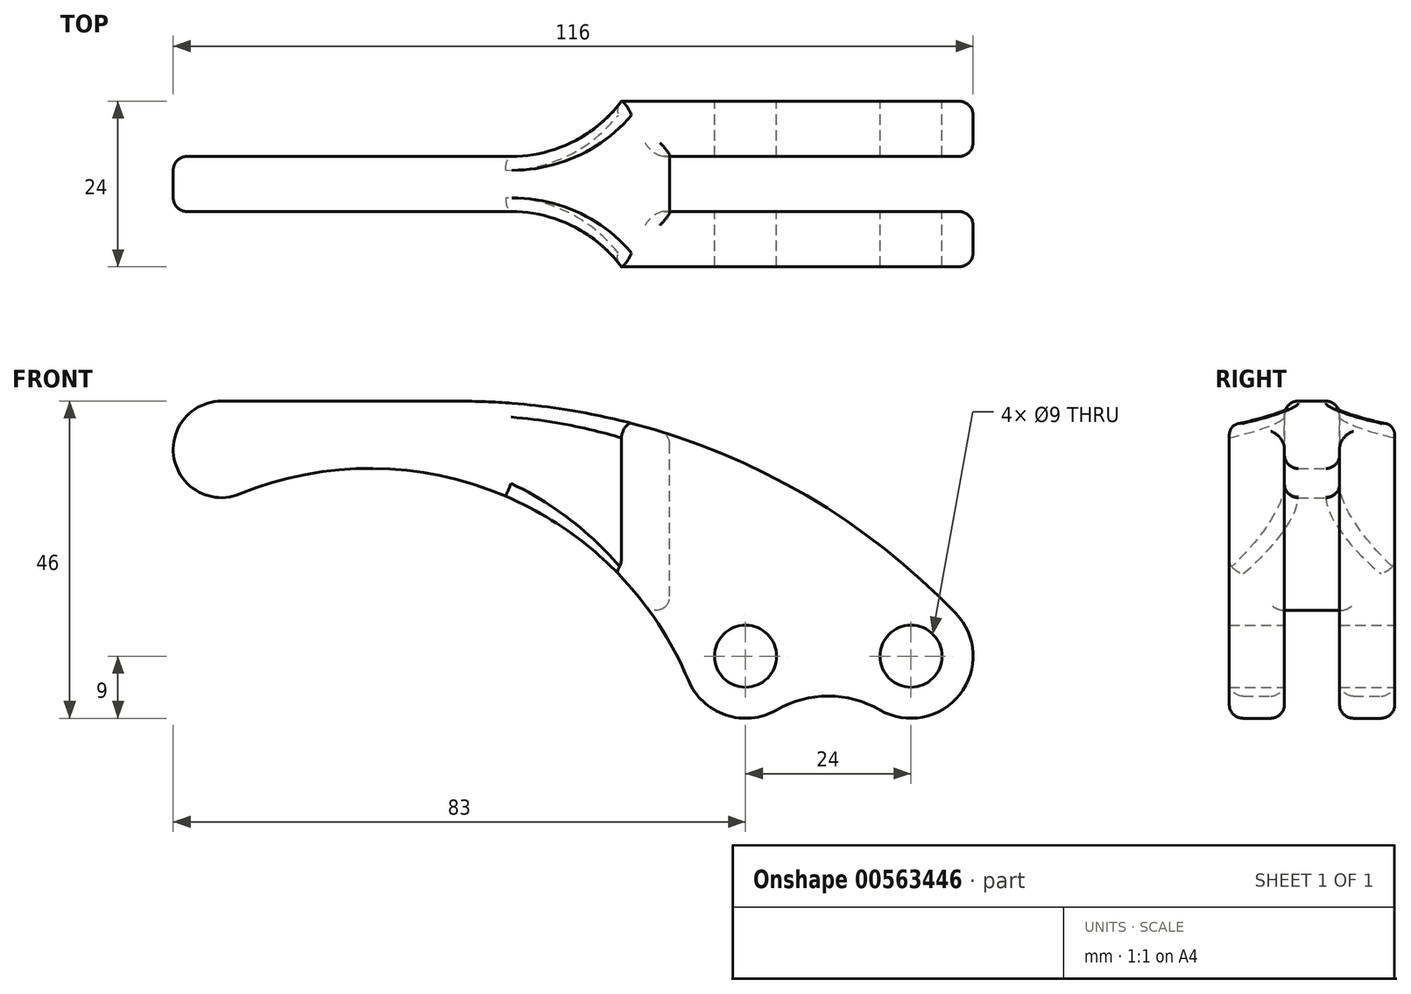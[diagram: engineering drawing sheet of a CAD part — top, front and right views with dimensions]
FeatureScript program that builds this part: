
annotation { "Feature Type Name" : "Feature", "Feature Type Description" : "" }
export const myFeature = defineFeature(function(context is Context, id is Id, definition is map)
    precondition{}
    {
        {
            var Q0;
            Q0=qCreatedBy(makeId("Front.planeOp"),FACE);
            var sketch = newSketch(context, id + "F0", { "sketchPlane" : qUnion([Q0])});
            skCircle(sketch, "E0", {"center": v(0, 0) * mm, "radius": 9 * mm});
            skCircle(sketch, "E1", {"center": v(-24, 0) * mm, "radius": 9 * mm});
            skCircle(sketch, "E2", {"center": v(-100, 30) * mm, "radius": 7 * mm});
            skArc(sketch, "E3", {"start": v(-4.5, -7.8) * mm, "mid": v(-12, -5.78) * mm, "end": v(-19.5, -7.8) * mm});
            skArc(sketch, "E4", {"start": v(-32.3, -3.47) * mm, "mid": v(-59.27, 23.42) * mm, "end": v(-97.35, 23.52) * mm});
            skLineSegment(sketch, "E5", {"start": v(-100, 37) * mm, "end": v(-65.67, 37) * mm});
            skArc(sketch, "E6", {"start": v(6.5, 6.23) * mm, "mid": v(-26.44, 28.99) * mm, "end": v(-65.67, 37) * mm});
            skCircle(sketch, "E7", {"center": v(-24, 0) * mm, "radius": 4.5 * mm});
            skCircle(sketch, "E8", {"center": v(0, 0) * mm, "radius": 4.5 * mm});
            skSolve(sketch);
        }
        {
            var Q0;
            Q0 = qSketchRegion(id + "F0", true);
            extrude(context, id + "F1", {"entities" : qUnion([Q0]), "depth" : 24 * mm, "offsetDistance" : 25 * mm});
        }
        {
            var Q0;
            Q0=qCreatedBy(makeId("Top.planeOp"),FACE);
            var sketch = newSketch(context, id + "F2", { "sketchPlane" : qUnion([Q0])});
            skLineSegment(sketch, "E9", {"start": v(9, 0) * mm, "end": v(9, -24) * mm});
            skLineSegment(sketch, "E10", {"start": v(-107, -24) * mm, "end": v(-107, 0) * mm});
            skLineSegment(sketch, "E11", {"start": v(-107, -12) * mm, "end": v(9, -12) * mm});
            skLineSegment(sketch, "E12", {"start": v(-35, -12) * mm, "end": v(-35, -8) * mm});
            skLineSegment(sketch, "E13", {"start": v(-35, -8) * mm, "end": v(9, -8) * mm});
            skLineSegment(sketch, "E14.MirrorCS", {"start": v(-35, -16) * mm, "end": v(9, -16) * mm});
            skLineSegment(sketch, "E15.MirrorCS", {"start": v(-35, -12) * mm, "end": v(-35, -16) * mm});
            skLineSegment(sketch, "E16.bottom", {"start": v(-107, 0) * mm, "end": v(-42, 0) * mm});
            skLineSegment(sketch, "E16.top", {"start": v(-107, -8) * mm, "end": v(-58, -8) * mm});
            skLineSegment(sketch, "E16.left", {"start": v(-107, 0) * mm, "end": v(-107, -8) * mm});
            skArc(sketch, "E17", {"start": v(-58, -8) * mm, "mid": v(-49.06, -5.89) * mm, "end": v(-42, 0) * mm});
            skArc(sketch, "E18.MirrorCS", {"start": v(-58, -16) * mm, "mid": v(-49.06, -18.11) * mm, "end": v(-42, -24) * mm});
            skLineSegment(sketch, "E19.MirrorCS", {"start": v(-107, -16) * mm, "end": v(-58, -16) * mm});
            skPoint(sketch, "E20.orphan", {"position": v(-42, -16) * mm});
            skLineSegment(sketch, "E21.MirrorCS", {"start": v(-107, -24) * mm, "end": v(-42, -24) * mm});
            skPoint(sketch, "E22.orphan", {"position": v(-42, -8) * mm});
            skSolve(sketch);
        }
        {
            var Q0;
            Q0 = qSketchRegion(id + "F2", true);
            extrude(context, id + "F3", {"entities" : qUnion([Q0]), "operationType" : NewBodyOperationType.REMOVE, "endBound" : BoundingType.THROUGH_ALL, "oppositeDirection" : true, "depth" : 25 * mm, "offsetDistance" : 25 * mm, "hasSecondDirection" : true, "secondDirectionBound" : SecondDirectionBoundingType.THROUGH_ALL, "secondDirectionOppositeDirection" : false, "secondDirectionDepth" : 25 * mm});
        }
        {
            var Q0;
            Q0=makeQuery(id+"F3.boolean.opBoolean","INTERSECT",EDGE,{"derivedFrom":[makeQuery(id+"F1.opExtrude","SWEPT_FACE",FACE,{"disambiguationData":[OSD([sQuery(id+"F0.wireOp",EDGE,"E6")])]}),makeQuery(id+"F3.opExtrude","SWEPT_FACE",FACE,{"disambiguationData":[OSD([sQuery(id+"F2.wireOp",EDGE,"E18.MirrorCS")])]})]});
            var Q1;
            Q1=makeQuery(id+"F1.opExtrude","CAP_EDGE",EDGE,{"disambiguationData":[OSD([sQuery(id+"F0.wireOp",EDGE,"E4")])],"isStart":false});
            var Q2;
            Q2=makeQuery(id+"F3.boolean.opBoolean","INTERSECT",EDGE,{"derivedFrom":[makeQuery(id+"F1.opExtrude","SWEPT_FACE",FACE,{"disambiguationData":[OSD([sQuery(id+"F0.wireOp",EDGE,"E6")])]}),makeQuery(id+"F3.opExtrude","SWEPT_FACE",FACE,{"disambiguationData":[OSD([sQuery(id+"F2.wireOp",EDGE,"E13")])]})]});
            var Q3;
            Q3=makeQuery(id+"F3.boolean.opBoolean","INTERSECT",EDGE,{"derivedFrom":[makeQuery(id+"F1.opExtrude","SWEPT_FACE",FACE,{"disambiguationData":[OSD([sQuery(id+"F0.wireOp",EDGE,"E6")])]}),makeQuery(id+"F3.opExtrude","SWEPT_FACE",FACE,{"disambiguationData":[OSD([sQuery(id+"F2.wireOp",EDGE,"E12"),sQuery(id+"F2.wireOp",EDGE,"E15.MirrorCS")])]})]});
            var Q4;
            Q4=makeQuery(id+"F3.boolean.opBoolean","INTERSECT",EDGE,{"derivedFrom":[makeQuery(id+"F1.opExtrude","SWEPT_FACE",FACE,{"disambiguationData":[OSD([sQuery(id+"F0.wireOp",EDGE,"E6")])]}),makeQuery(id+"F3.opExtrude","SWEPT_FACE",FACE,{"disambiguationData":[OSD([sQuery(id+"F2.wireOp",EDGE,"E14.MirrorCS")])]})]});
            var Q5;
            Q5=makeQuery(id+"F3.boolean.opBoolean","INTERSECT",EDGE,{"derivedFrom":[makeQuery(id+"F1.opExtrude","SWEPT_FACE",FACE,{"disambiguationData":[OSD([sQuery(id+"F0.wireOp",EDGE,"E4")])]}),makeQuery(id+"F3.opExtrude","SWEPT_FACE",FACE,{"disambiguationData":[OSD([sQuery(id+"F2.wireOp",EDGE,"E12"),sQuery(id+"F2.wireOp",EDGE,"E15.MirrorCS")])]})]});
            var Q6;
            Q6=makeQuery(id+"F3.boolean.opBoolean","INTERSECT",EDGE,{"derivedFrom":[makeQuery(id+"F1.opExtrude","SWEPT_FACE",FACE,{"disambiguationData":[OSD([sQuery(id+"F0.wireOp",EDGE,"E4")])]}),makeQuery(id+"F3.opExtrude","SWEPT_FACE",FACE,{"disambiguationData":[OSD([sQuery(id+"F2.wireOp",EDGE,"E16.top")])]})]});
            var Q7;
            Q7=makeQuery(id+"F1.opExtrude","CAP_EDGE",EDGE,{"disambiguationData":[OSD([sQuery(id+"F0.wireOp",EDGE,"E6")])],"isStart":true});
            fillet(context, id + "F4", {"entities" : qUnion([Q0, Q1, Q2, Q3, Q4, Q5, Q6, Q7]), "radius" : 2 * mm, "tangentPropagation" : true, "allowEdgeOverflow" : false});
        }
    });
